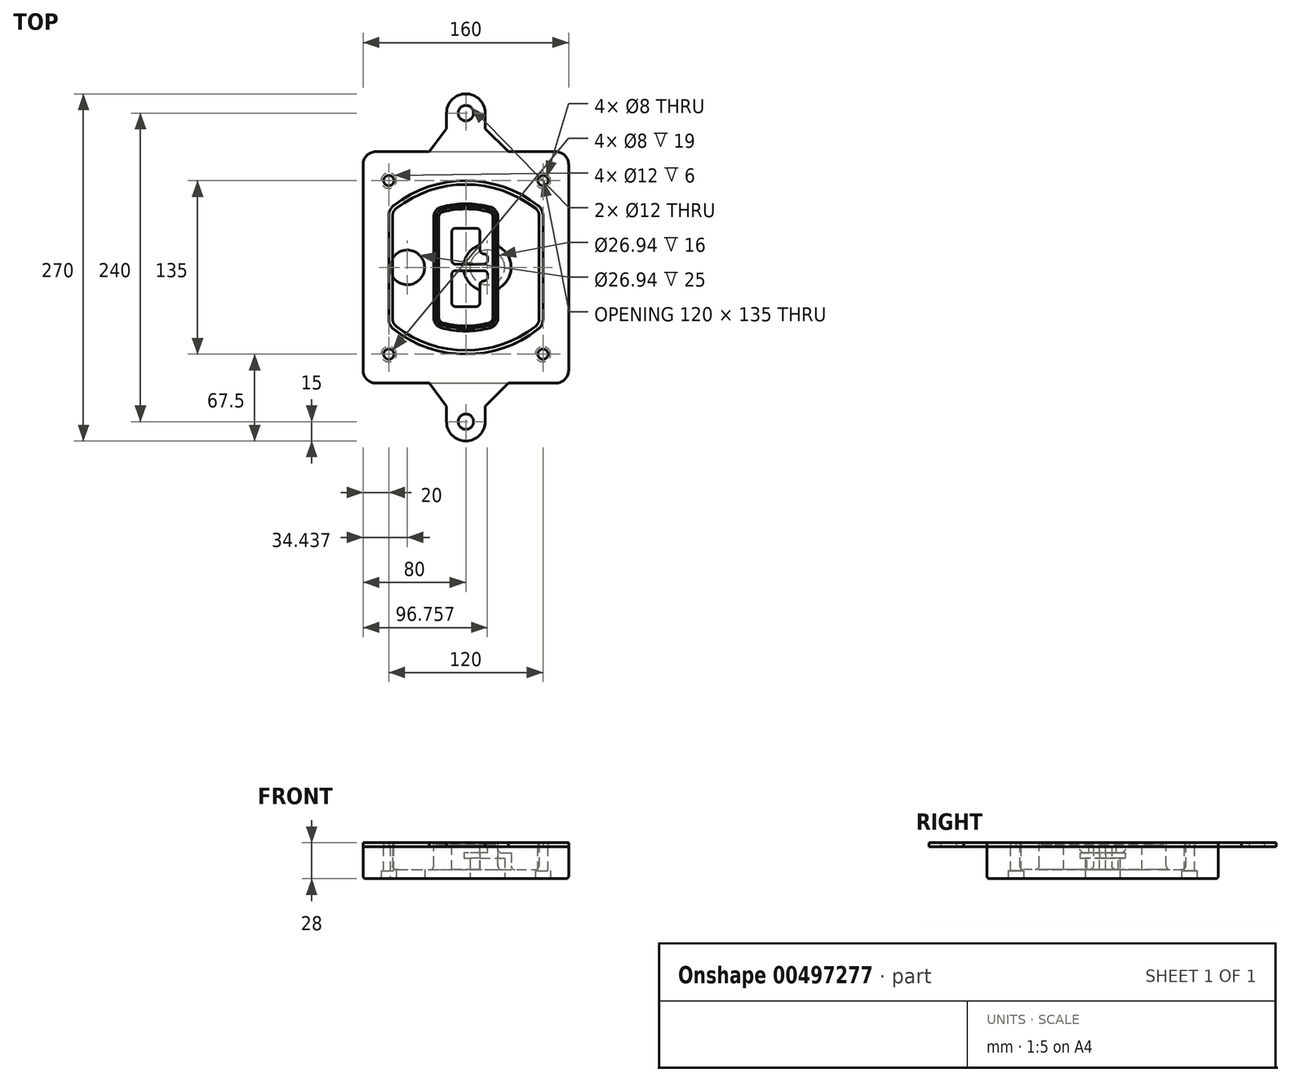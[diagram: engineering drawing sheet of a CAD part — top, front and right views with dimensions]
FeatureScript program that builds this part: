
annotation { "Feature Type Name" : "Feature", "Feature Type Description" : "" }
export const myFeature = defineFeature(function(context is Context, id is Id, definition is map)
    precondition{}
    {
        {
            var Q0;
            Q0=qCreatedBy(makeId("Top.planeOp"),FACE);
            var sketch = newSketch(context, id + "F0", { "sketchPlane" : qUnion([Q0])});
            skPoint(sketch, "E0.rect.middle", {"position": v(0, 0) * mm});
            skLineSegment(sketch, "E1.bottom", {"start": v(-70, -90) * mm, "end": v(70, -90) * mm});
            skLineSegment(sketch, "E1.top", {"start": v(-70, 90) * mm, "end": v(70, 90) * mm});
            skLineSegment(sketch, "E1.left", {"start": v(-80, -80) * mm, "end": v(-80, 80) * mm});
            skLineSegment(sketch, "E1.right", {"start": v(80, -80) * mm, "end": v(80, 80) * mm});
            skLineSegment(sketch, "E2", {"start": v(-80, 90) * mm, "end": v(80, -90) * mm, "construction": true});
            skLineSegment(sketch, "E3", {"start": v(80, 90) * mm, "end": v(-80, -90) * mm, "construction": true});
            skCircle(sketch, "E4", {"center": v(-60, 67.5) * mm, "radius": 4 * mm});
            skCircle(sketch, "E5", {"center": v(60, 67.5) * mm, "radius": 4 * mm});
            skCircle(sketch, "E6", {"center": v(60, -67.5) * mm, "radius": 4 * mm});
            skCircle(sketch, "E7", {"center": v(-60, -67.5) * mm, "radius": 4 * mm});
            skLineSegment(sketch, "E8", {"start": v(-60, 67.5) * mm, "end": v(60, 67.5) * mm, "construction": true});
            skLineSegment(sketch, "E9", {"start": v(60, 67.5) * mm, "end": v(60, -67.5) * mm, "construction": true});
            skLineSegment(sketch, "E10", {"start": v(60, -67.5) * mm, "end": v(-60, -67.5) * mm, "construction": true});
            skLineSegment(sketch, "E11", {"start": v(-60, -67.5) * mm, "end": v(-60, 67.5) * mm, "construction": true});
            skLineSegment(sketch, "E12", {"start": v(-60, 40.3) * mm, "end": v(-60, -40.3) * mm});
            skLineSegment(sketch, "E13", {"start": v(60, 40.3) * mm, "end": v(60, -40.3) * mm});
            skArc(sketch, "E14", {"start": v(56.15, 48.18) * mm, "mid": v(0, 67.5) * mm, "end": v(-56.15, 48.18) * mm});
            skArc(sketch, "E15", {"start": v(-56.15, -48.18) * mm, "mid": v(0, -67.5) * mm, "end": v(56.15, -48.18) * mm});
            skLineSegment(sketch, "E16", {"start": v(-60, 0) * mm, "end": v(60, 0) * mm, "construction": true});
            skPoint(sketch, "E17.visualSharp", {"position": v(-60, -45) * mm});
            skArc(sketch, "E17.filletArc", {"start": v(-60, -40.3) * mm, "mid": v(-58.99, -44.68) * mm, "end": v(-56.15, -48.18) * mm});
            skPoint(sketch, "E18.visualSharp", {"position": v(-60, 45) * mm});
            skArc(sketch, "E18.filletArc", {"start": v(-56.15, 48.18) * mm, "mid": v(-58.99, 44.68) * mm, "end": v(-60, 40.3) * mm});
            skPoint(sketch, "E19.visualSharp", {"position": v(60, 45) * mm});
            skArc(sketch, "E19.filletArc", {"start": v(60, 40.3) * mm, "mid": v(58.99, 44.68) * mm, "end": v(56.15, 48.18) * mm});
            skPoint(sketch, "E20.visualSharp", {"position": v(60, -45) * mm});
            skArc(sketch, "E20.filletArc", {"start": v(56.15, -48.18) * mm, "mid": v(58.99, -44.68) * mm, "end": v(60, -40.3) * mm});
            skPoint(sketch, "E21.visualSharp", {"position": v(-80, 90) * mm});
            skArc(sketch, "E21.filletArc", {"start": v(-70, 90) * mm, "mid": v(-77.07, 87.07) * mm, "end": v(-80, 80) * mm});
            skPoint(sketch, "E22.visualSharp", {"position": v(80, 90) * mm});
            skArc(sketch, "E22.filletArc", {"start": v(80, 80) * mm, "mid": v(77.07, 87.07) * mm, "end": v(70, 90) * mm});
            skPoint(sketch, "E23.visualSharp", {"position": v(80, -90) * mm});
            skArc(sketch, "E23.filletArc", {"start": v(70, -90) * mm, "mid": v(77.07, -87.07) * mm, "end": v(80, -80) * mm});
            skPoint(sketch, "E24.visualSharp", {"position": v(-80, -90) * mm});
            skArc(sketch, "E24.filletArc", {"start": v(-80, -80) * mm, "mid": v(-77.07, -87.07) * mm, "end": v(-70, -90) * mm});
            skArc(sketch, "E25.0", {"start": v(57, 40.3) * mm, "mid": v(56.3, 43.36) * mm, "end": v(54.3, 45.81) * mm});
            skLineSegment(sketch, "E25.1", {"start": v(57, 40.3) * mm, "end": v(57, -40.3) * mm});
            skArc(sketch, "E25.2", {"start": v(54.3, -45.81) * mm, "mid": v(56.3, -43.36) * mm, "end": v(57, -40.3) * mm});
            skArc(sketch, "E25.3", {"start": v(-54.3, -45.81) * mm, "mid": v(0, -64.5) * mm, "end": v(54.3, -45.81) * mm});
            skArc(sketch, "E25.4", {"start": v(-57, -40.3) * mm, "mid": v(-56.3, -43.36) * mm, "end": v(-54.3, -45.81) * mm});
            skArc(sketch, "E25.5", {"start": v(54.3, 45.81) * mm, "mid": v(0, 64.5) * mm, "end": v(-54.3, 45.81) * mm});
            skLineSegment(sketch, "E25.6", {"start": v(-57, 40.3) * mm, "end": v(-57, -40.3) * mm});
            skArc(sketch, "E25.7", {"start": v(-54.3, 45.81) * mm, "mid": v(-56.3, 43.36) * mm, "end": v(-57, 40.3) * mm});
            skArc(sketch, "E26.0", {"start": v(-58.62, 51.33) * mm, "mid": v(-62.58, 46.43) * mm, "end": v(-64, 40.3) * mm});
            skArc(sketch, "E26.1", {"start": v(58.62, 51.33) * mm, "mid": v(0, 71.5) * mm, "end": v(-58.62, 51.33) * mm});
            skArc(sketch, "E26.2", {"start": v(64, 40.3) * mm, "mid": v(62.58, 46.43) * mm, "end": v(58.62, 51.33) * mm});
            skLineSegment(sketch, "E26.3", {"start": v(64, 40.3) * mm, "end": v(64, -40.3) * mm});
            skArc(sketch, "E26.4", {"start": v(58.62, -51.33) * mm, "mid": v(62.58, -46.43) * mm, "end": v(64, -40.3) * mm});
            skLineSegment(sketch, "E26.5", {"start": v(-64, 40.3) * mm, "end": v(-64, -40.3) * mm});
            skArc(sketch, "E26.6", {"start": v(-58.62, -51.33) * mm, "mid": v(0, -71.5) * mm, "end": v(58.62, -51.33) * mm});
            skArc(sketch, "E26.7", {"start": v(-64, -40.3) * mm, "mid": v(-62.58, -46.43) * mm, "end": v(-58.62, -51.33) * mm});
            skSolve(sketch);
        }
        {
            var Q0;
            Q0=makeQuery(id+"F0.imprint","IMPRINT",FACE,{"disambiguationData":[TD([[makeQuery(id+"F0.imprint","IMPRINT",EDGE,{"derivedFrom":sQuery(id+"F0.wireOp",EDGE,"E1.bottom")}),1.0]])]});
            var Q1;
            Q1=makeQuery(id+"F0.imprint","IMPRINT",FACE,{"disambiguationData":[TD([[makeQuery(id+"F0.imprint","IMPRINT",EDGE,{"derivedFrom":sQuery(id+"F0.wireOp",EDGE,"E12")}),1.0]])]});
            var Q2;
            Q2=makeQuery(id+"F0.imprint","IMPRINT",FACE,{"disambiguationData":[TD([[makeQuery(id+"F0.imprint","IMPRINT",EDGE,{"derivedFrom":sQuery(id+"F0.wireOp",EDGE,"E25.0")}),1.0]])]});
            var Q3;
            Q3=makeQuery(id+"F0.imprint","IMPRINT",FACE,{"disambiguationData":[TD([[makeQuery(id+"F0.imprint","IMPRINT",EDGE,{"derivedFrom":sQuery(id+"F0.wireOp",EDGE,"E12")}),-1.0]])]});
            extrude(context, id + "F1", {"entities" : qUnion([Q0, Q1, Q2, Q3]), "oppositeDirection" : true, "depth" : 25 * mm});
        }
        {
            var Q0;
            Q0=makeQuery(id+"F0.imprint","IMPRINT",FACE,{"disambiguationData":[TD([[makeQuery(id+"F0.imprint","IMPRINT",EDGE,{"derivedFrom":sQuery(id+"F0.wireOp",EDGE,"E12")}),1.0]])]});
            extrude(context, id + "F2", {"entities" : qUnion([Q0]), "operationType" : NewBodyOperationType.ADD, "depth" : 3 * mm});
        }
        {
            var Q0;
            Q0=makeQuery(id+"F0.imprint","IMPRINT",FACE,{"disambiguationData":[TD([[makeQuery(id+"F0.imprint","IMPRINT",EDGE,{"derivedFrom":sQuery(id+"F0.wireOp",EDGE,"E25.0")}),1.0]])]});
            extrude(context, id + "F3", {"entities" : qUnion([Q0]), "operationType" : NewBodyOperationType.REMOVE, "oppositeDirection" : true, "depth" : 18 * mm});
        }
        {
            var Q0;
            Q0=makeQuery(id+"F2.opExtrude","CAP_FACE",FACE,{"disambiguationData":[OSD([sQuery(id+"F0.wireOp",EDGE,"E12"),sQuery(id+"F0.wireOp",EDGE,"E13"),sQuery(id+"F0.wireOp",EDGE,"E14"),sQuery(id+"F0.wireOp",EDGE,"E15"),sQuery(id+"F0.wireOp",EDGE,"E17.filletArc"),sQuery(id+"F0.wireOp",EDGE,"E18.filletArc"),sQuery(id+"F0.wireOp",EDGE,"E19.filletArc"),sQuery(id+"F0.wireOp",EDGE,"E20.filletArc"),sQuery(id+"F0.wireOp",EDGE,"E25.0"),sQuery(id+"F0.wireOp",EDGE,"E25.1"),sQuery(id+"F0.wireOp",EDGE,"E25.2"),sQuery(id+"F0.wireOp",EDGE,"E25.3"),sQuery(id+"F0.wireOp",EDGE,"E25.4"),sQuery(id+"F0.wireOp",EDGE,"E25.5"),sQuery(id+"F0.wireOp",EDGE,"E25.6"),sQuery(id+"F0.wireOp",EDGE,"E25.7")])],"isStart":false});
            var sketch = newSketch(context, id + "F4", { "sketchPlane" : qUnion([Q0])});
            skArc(sketch, "E27.0", {"start": v(-19.08, -46.97) * mm, "mid": v(0, -49.5) * mm, "end": v(19.08, -46.97) * mm});
            skArc(sketch, "E28.0", {"start": v(19.08, 46.97) * mm, "mid": v(0, 49.5) * mm, "end": v(-19.08, 46.97) * mm});
            skLineSegment(sketch, "E29", {"start": v(-25, 39.25) * mm, "end": v(-25, -39.25) * mm});
            skLineSegment(sketch, "E30", {"start": v(25, 39.25) * mm, "end": v(25, -39.25) * mm});
            skLineSegment(sketch, "E31", {"start": v(-25, 45.1) * mm, "end": v(25, 45.1) * mm, "construction": true});
            skLineSegment(sketch, "E32", {"start": v(-25, -45.1) * mm, "end": v(25, -45.1) * mm, "construction": true});
            skPoint(sketch, "E33.visualSharp", {"position": v(-25, 45.1) * mm});
            skArc(sketch, "E33.filletArc", {"start": v(-19.08, 46.97) * mm, "mid": v(-23.35, 44.11) * mm, "end": v(-25, 39.25) * mm});
            skPoint(sketch, "E34.visualSharp", {"position": v(25, 45.1) * mm});
            skArc(sketch, "E34.filletArc", {"start": v(25, 39.25) * mm, "mid": v(23.35, 44.11) * mm, "end": v(19.08, 46.97) * mm});
            skPoint(sketch, "E35.visualSharp", {"position": v(25, -45.1) * mm});
            skArc(sketch, "E35.filletArc", {"start": v(19.08, -46.97) * mm, "mid": v(23.35, -44.11) * mm, "end": v(25, -39.25) * mm});
            skPoint(sketch, "E36.visualSharp", {"position": v(-25, -45.1) * mm});
            skArc(sketch, "E36.filletArc", {"start": v(-25, -39.25) * mm, "mid": v(-23.35, -44.11) * mm, "end": v(-19.08, -46.97) * mm});
            skArc(sketch, "E37.0", {"start": v(54.3, 45.81) * mm, "mid": v(0, 64.5) * mm, "end": v(-54.3, 45.81) * mm});
            skArc(sketch, "E37.1", {"start": v(-54.3, 45.81) * mm, "mid": v(-56.3, 43.36) * mm, "end": v(-57, 40.3) * mm});
            skLineSegment(sketch, "E37.2", {"start": v(-57, 40.3) * mm, "end": v(-57, -40.3) * mm});
            skArc(sketch, "E37.3", {"start": v(-57, -40.3) * mm, "mid": v(-56.3, -43.36) * mm, "end": v(-54.3, -45.81) * mm});
            skArc(sketch, "E37.4", {"start": v(-54.3, -45.81) * mm, "mid": v(0, -64.5) * mm, "end": v(54.3, -45.81) * mm});
            skArc(sketch, "E37.5", {"start": v(54.3, -45.81) * mm, "mid": v(56.3, -43.36) * mm, "end": v(57, -40.3) * mm});
            skLineSegment(sketch, "E37.6", {"start": v(57, 40.3) * mm, "end": v(57, -40.3) * mm});
            skArc(sketch, "E37.7", {"start": v(57, 40.3) * mm, "mid": v(56.3, 43.36) * mm, "end": v(54.3, 45.81) * mm});
            skLineSegment(sketch, "E38.0", {"start": v(23, 39.25) * mm, "end": v(23, -39.25) * mm});
            skArc(sketch, "E38.1", {"start": v(18.56, -45.04) * mm, "mid": v(21.76, -42.9) * mm, "end": v(23, -39.25) * mm});
            skArc(sketch, "E38.2", {"start": v(-18.56, -45.04) * mm, "mid": v(0, -47.5) * mm, "end": v(18.56, -45.04) * mm});
            skArc(sketch, "E38.3", {"start": v(-23, -39.25) * mm, "mid": v(-21.76, -42.9) * mm, "end": v(-18.56, -45.04) * mm});
            skLineSegment(sketch, "E38.4", {"start": v(-23, 39.25) * mm, "end": v(-23, -39.25) * mm});
            skArc(sketch, "E38.5", {"start": v(23, 39.25) * mm, "mid": v(21.76, 42.9) * mm, "end": v(18.56, 45.04) * mm});
            skArc(sketch, "E38.6", {"start": v(-18.56, 45.04) * mm, "mid": v(-21.76, 42.9) * mm, "end": v(-23, 39.25) * mm});
            skArc(sketch, "E38.7", {"start": v(18.56, 45.04) * mm, "mid": v(0, 47.5) * mm, "end": v(-18.56, 45.04) * mm});
            skArc(sketch, "E39.0", {"start": v(21, 39.25) * mm, "mid": v(20.18, 41.68) * mm, "end": v(18.04, 43.1) * mm});
            skLineSegment(sketch, "E39.1", {"start": v(21, 39.25) * mm, "end": v(21, -39.25) * mm});
            skArc(sketch, "E39.2", {"start": v(18.04, -43.1) * mm, "mid": v(20.18, -41.68) * mm, "end": v(21, -39.25) * mm});
            skArc(sketch, "E39.3", {"start": v(-18.04, -43.1) * mm, "mid": v(0, -45.5) * mm, "end": v(18.04, -43.1) * mm});
            skArc(sketch, "E39.4", {"start": v(-21, -39.25) * mm, "mid": v(-20.18, -41.68) * mm, "end": v(-18.04, -43.1) * mm});
            skArc(sketch, "E39.5", {"start": v(18.04, 43.1) * mm, "mid": v(0, 45.5) * mm, "end": v(-18.04, 43.1) * mm});
            skLineSegment(sketch, "E39.6", {"start": v(-21, 39.25) * mm, "end": v(-21, -39.25) * mm});
            skArc(sketch, "E39.7", {"start": v(-18.04, 43.1) * mm, "mid": v(-20.18, 41.68) * mm, "end": v(-21, 39.25) * mm});
            skLineSegment(sketch, "E40", {"start": v(-25, 0) * mm, "end": v(25, 0) * mm, "construction": true});
            skLineSegment(sketch, "E41", {"start": v(-11, 5.5) * mm, "end": v(-11, 27.5) * mm});
            skLineSegment(sketch, "E42", {"start": v(-8, 30.5) * mm, "end": v(8, 30.5) * mm});
            skLineSegment(sketch, "E43", {"start": v(11, 27.5) * mm, "end": v(11, 13.5) * mm});
            skLineSegment(sketch, "E44", {"start": v(14, 10.5) * mm, "end": v(14, 10.5) * mm});
            skLineSegment(sketch, "E45", {"start": v(17, 7.5) * mm, "end": v(17, 5.5) * mm});
            skLineSegment(sketch, "E46", {"start": v(14, 2.5) * mm, "end": v(-8, 2.5) * mm});
            skPoint(sketch, "E47.visualSharp", {"position": v(-11, 30.5) * mm});
            skArc(sketch, "E47.filletArc", {"start": v(-8, 30.5) * mm, "mid": v(-10.12, 29.62) * mm, "end": v(-11, 27.5) * mm});
            skPoint(sketch, "E48.visualSharp", {"position": v(11, 30.5) * mm});
            skArc(sketch, "E48.filletArc", {"start": v(11, 27.5) * mm, "mid": v(10.12, 29.62) * mm, "end": v(8, 30.5) * mm});
            skPoint(sketch, "E49.visualSharp", {"position": v(11, 10.5) * mm});
            skArc(sketch, "E49.filletArc", {"start": v(11, 13.5) * mm, "mid": v(11.88, 11.38) * mm, "end": v(14, 10.5) * mm});
            skPoint(sketch, "E50.visualSharp", {"position": v(17, 10.5) * mm});
            skArc(sketch, "E50.filletArc", {"start": v(17, 7.5) * mm, "mid": v(16.12, 9.62) * mm, "end": v(14, 10.5) * mm});
            skPoint(sketch, "E51.visualSharp", {"position": v(17, 2.5) * mm});
            skArc(sketch, "E51.filletArc", {"start": v(14, 2.5) * mm, "mid": v(16.12, 3.38) * mm, "end": v(17, 5.5) * mm});
            skPoint(sketch, "E52.visualSharp", {"position": v(-11, 2.5) * mm});
            skArc(sketch, "E52.filletArc", {"start": v(-11, 5.5) * mm, "mid": v(-10.12, 3.38) * mm, "end": v(-8, 2.5) * mm});
            skLineSegment(sketch, "E53.0.MirrorCS", {"start": v(14, -2.5) * mm, "end": v(-8, -2.5) * mm});
            skArc(sketch, "E54.0.MirrorCS", {"start": v(-11, -5.5) * mm, "mid": v(-10.12, -3.38) * mm, "end": v(-8, -2.5) * mm});
            skLineSegment(sketch, "E55.0.MirrorCS", {"start": v(-11, -5.5) * mm, "end": v(-11, -27.5) * mm});
            skArc(sketch, "E56.0.MirrorCS", {"start": v(-8, -30.5) * mm, "mid": v(-10.12, -29.62) * mm, "end": v(-11, -27.5) * mm});
            skLineSegment(sketch, "E57.0.MirrorCS", {"start": v(-8, -30.5) * mm, "end": v(8, -30.5) * mm});
            skArc(sketch, "E58.0.MirrorCS", {"start": v(11, -27.5) * mm, "mid": v(10.12, -29.62) * mm, "end": v(8, -30.5) * mm});
            skLineSegment(sketch, "E59.0.MirrorCS", {"start": v(11, -27.5) * mm, "end": v(11, -13.5) * mm});
            skArc(sketch, "E60.0.MirrorCS", {"start": v(11, -13.5) * mm, "mid": v(11.88, -11.38) * mm, "end": v(14, -10.5) * mm});
            skArc(sketch, "E61.0.MirrorCS", {"start": v(17, -7.5) * mm, "mid": v(16.12, -9.62) * mm, "end": v(14, -10.5) * mm});
            skLineSegment(sketch, "E62.0.MirrorCS", {"start": v(17, -7.5) * mm, "end": v(17, -5.5) * mm});
            skArc(sketch, "E63.0.MirrorCS", {"start": v(14, -2.5) * mm, "mid": v(16.12, -3.38) * mm, "end": v(17, -5.5) * mm});
            skSolve(sketch);
        }
        {
            var Q0;
            Q0=makeQuery(id+"F4.imprint","IMPRINT",FACE,{"disambiguationData":[TD([[makeQuery(id+"F4.imprint","IMPRINT",EDGE,{"derivedFrom":sQuery(id+"F4.wireOp",EDGE,"E27.0")}),1.0]])]});
            var Q1;
            Q1=makeQuery(id+"F4.imprint","IMPRINT",FACE,{"disambiguationData":[TD([[makeQuery(id+"F4.imprint","IMPRINT",EDGE,{"derivedFrom":sQuery(id+"F4.wireOp",EDGE,"E38.0")}),-1.0]])]});
            var Q2;
            Q2=makeQuery(id+"F4.imprint","IMPRINT",FACE,{"disambiguationData":[TD([[makeQuery(id+"F4.imprint","IMPRINT",EDGE,{"derivedFrom":sQuery(id+"F4.wireOp",EDGE,"E39.0")}),1.0]])]});
            extrude(context, id + "F5", {"entities" : qUnion([Q0, Q1, Q2]), "operationType" : NewBodyOperationType.ADD, "endBound" : BoundingType.UP_TO_NEXT, "oppositeDirection" : true, "depth" : 25 * mm});
        }
        {
            var Q0;
            Q0=makeQuery(id+"F4.imprint","IMPRINT",FACE,{"disambiguationData":[TD([[makeQuery(id+"F4.imprint","IMPRINT",EDGE,{"derivedFrom":sQuery(id+"F4.wireOp",EDGE,"E38.0")}),-1.0]])]});
            extrude(context, id + "F6", {"entities" : qUnion([Q0]), "operationType" : NewBodyOperationType.REMOVE, "oppositeDirection" : true, "depth" : 2 * mm});
        }
        {
            var Q0;
            Q0=makeQuery(id+"F1.opExtrude","CAP_FACE",FACE,{"disambiguationData":[OSD([sQuery(id+"F0.wireOp",EDGE,"E1.bottom"),sQuery(id+"F0.wireOp",EDGE,"E1.top"),sQuery(id+"F0.wireOp",EDGE,"E1.left"),sQuery(id+"F0.wireOp",EDGE,"E1.right"),sQuery(id+"F0.wireOp",EDGE,"E4"),sQuery(id+"F0.wireOp",EDGE,"E5"),sQuery(id+"F0.wireOp",EDGE,"E6"),sQuery(id+"F0.wireOp",EDGE,"E7"),sQuery(id+"F0.wireOp",EDGE,"E21.filletArc"),sQuery(id+"F0.wireOp",EDGE,"E22.filletArc"),sQuery(id+"F0.wireOp",EDGE,"E23.filletArc"),sQuery(id+"F0.wireOp",EDGE,"E24.filletArc")])],"isStart":false});
            var sketch = newSketch(context, id + "F7", { "sketchPlane" : qUnion([Q0])});
            skCircle(sketch, "E64", {"center": v(16.76, 0) * mm, "radius": 13.47 * mm});
            skCircle(sketch, "E65", {"center": v(-45.56, 0) * mm, "radius": 13.47 * mm});
            skLineSegment(sketch, "E66", {"start": v(80, 0) * mm, "end": v(-80, 0) * mm});
            skCircle(sketch, "E67", {"center": v(16.76, 0) * mm, "radius": 18.47 * mm});
            skCircle(sketch, "E68", {"center": v(60, -67.5) * mm, "radius": 6 * mm});
            skCircle(sketch, "E69", {"center": v(-60, -67.5) * mm, "radius": 6 * mm});
            skCircle(sketch, "E70", {"center": v(-60, 67.5) * mm, "radius": 6 * mm});
            skCircle(sketch, "E71", {"center": v(60, 67.5) * mm, "radius": 6 * mm});
            skSolve(sketch);
        }
        {
            var Q0;
            {var subQ1=sQuery(id+"F7.wireOp",EDGE,"E66");var subQ4=sQuery(id+"F7.wireOp",EDGE,"E64");var subQ6=makeQuery(id+"F7.imprint","INTERSECT",VERTEX,{"disambiguationData":[OD(0.0)],"derivedFrom":[subQ4,subQ1]});Q0=makeQuery(id+"F7.imprint","IMPRINT",FACE,{"disambiguationData":[TD([[makeQuery(id+"F7.imprint","IMPRINT",EDGE,{"disambiguationData":[TD([[subQ6,-1.0]])],"derivedFrom":subQ4}),-1.0]])]});}
            var Q1;
            {var subQ0=sQuery(id+"F7.wireOp",EDGE,"E66");var subQ1=sQuery(id+"F7.wireOp",EDGE,"E64");var subQ3=makeQuery(id+"F7.imprint","INTERSECT",VERTEX,{"disambiguationData":[OD(0.0)],"derivedFrom":[subQ1,subQ0]});Q1=makeQuery(id+"F7.imprint","IMPRINT",FACE,{"disambiguationData":[TD([[makeQuery(id+"F7.imprint","IMPRINT",EDGE,{"disambiguationData":[TD([[subQ3,-1.0]])],"derivedFrom":subQ1}),1.0]])]});}
            var Q2;
            {var subQ0=sQuery(id+"F7.wireOp",EDGE,"E66");var subQ1=sQuery(id+"F7.wireOp",EDGE,"E64");var subQ3=makeQuery(id+"F7.imprint","INTERSECT",VERTEX,{"disambiguationData":[OD(0.0)],"derivedFrom":[subQ1,subQ0]});Q2=makeQuery(id+"F7.imprint","IMPRINT",FACE,{"disambiguationData":[TD([[makeQuery(id+"F7.imprint","IMPRINT",EDGE,{"disambiguationData":[TD([[subQ3,1.0]])],"derivedFrom":subQ1}),1.0]])]});}
            var Q3;
            {var subQ1=sQuery(id+"F7.wireOp",EDGE,"E66");var subQ4=sQuery(id+"F7.wireOp",EDGE,"E64");var subQ6=makeQuery(id+"F7.imprint","INTERSECT",VERTEX,{"disambiguationData":[OD(0.0)],"derivedFrom":[subQ4,subQ1]});Q3=makeQuery(id+"F7.imprint","IMPRINT",FACE,{"disambiguationData":[TD([[makeQuery(id+"F7.imprint","IMPRINT",EDGE,{"disambiguationData":[TD([[subQ6,1.0]])],"derivedFrom":subQ4}),-1.0]])]});}
            extrude(context, id + "F8", {"entities" : qUnion([Q0, Q1, Q2, Q3]), "operationType" : NewBodyOperationType.ADD, "oppositeDirection" : true, "depth" : 20 * mm});
        }
        {
            var Q0;
            {var subQ0=sQuery(id+"F7.wireOp",EDGE,"E66");var subQ1=sQuery(id+"F7.wireOp",EDGE,"E64");var subQ3=makeQuery(id+"F7.imprint","INTERSECT",VERTEX,{"disambiguationData":[OD(0.0)],"derivedFrom":[subQ1,subQ0]});Q0=makeQuery(id+"F7.imprint","IMPRINT",FACE,{"disambiguationData":[TD([[makeQuery(id+"F7.imprint","IMPRINT",EDGE,{"disambiguationData":[TD([[subQ3,-1.0]])],"derivedFrom":subQ1}),1.0]])]});}
            var Q1;
            {var subQ0=sQuery(id+"F7.wireOp",EDGE,"E66");var subQ1=sQuery(id+"F7.wireOp",EDGE,"E64");var subQ3=makeQuery(id+"F7.imprint","INTERSECT",VERTEX,{"disambiguationData":[OD(0.0)],"derivedFrom":[subQ1,subQ0]});Q1=makeQuery(id+"F7.imprint","IMPRINT",FACE,{"disambiguationData":[TD([[makeQuery(id+"F7.imprint","IMPRINT",EDGE,{"disambiguationData":[TD([[subQ3,1.0]])],"derivedFrom":subQ1}),1.0]])]});}
            extrude(context, id + "F9", {"entities" : qUnion([Q0, Q1]), "operationType" : NewBodyOperationType.REMOVE, "oppositeDirection" : true, "depth" : 16 * mm});
        }
        {
            var Q0;
            {var subQ0=sQuery(id+"F7.wireOp",EDGE,"E66");var subQ1=sQuery(id+"F7.wireOp",EDGE,"E65");var subQ3=makeQuery(id+"F7.imprint","INTERSECT",VERTEX,{"disambiguationData":[OD(0.0)],"derivedFrom":[subQ1,subQ0]});Q0=makeQuery(id+"F7.imprint","IMPRINT",FACE,{"disambiguationData":[TD([[makeQuery(id+"F7.imprint","IMPRINT",EDGE,{"disambiguationData":[TD([[subQ3,-1.0]])],"derivedFrom":subQ1}),1.0]])]});}
            var Q1;
            {var subQ0=sQuery(id+"F7.wireOp",EDGE,"E66");var subQ1=sQuery(id+"F7.wireOp",EDGE,"E65");var subQ3=makeQuery(id+"F7.imprint","INTERSECT",VERTEX,{"disambiguationData":[OD(0.0)],"derivedFrom":[subQ1,subQ0]});Q1=makeQuery(id+"F7.imprint","IMPRINT",FACE,{"disambiguationData":[TD([[makeQuery(id+"F7.imprint","IMPRINT",EDGE,{"disambiguationData":[TD([[subQ3,1.0]])],"derivedFrom":subQ1}),1.0]])]});}
            extrude(context, id + "F10", {"entities" : qUnion([Q0, Q1]), "operationType" : NewBodyOperationType.REMOVE, "oppositeDirection" : true, "depth" : 25 * mm});
        }
        {
            var Q0;
            Q0=makeQuery(id+"F7.imprint","IMPRINT",FACE,{"disambiguationData":[TD([[makeQuery(id+"F7.imprint","IMPRINT",EDGE,{"derivedFrom":sQuery(id+"F7.wireOp",EDGE,"E68")}),1.0]])]});
            var Q1;
            Q1=makeQuery(id+"F7.imprint","IMPRINT",FACE,{"disambiguationData":[TD([[makeQuery(id+"F7.imprint","IMPRINT",EDGE,{"derivedFrom":makeQuery(id+"F1.opExtrude","CAP_EDGE",EDGE,{"disambiguationData":[OSD([sQuery(id+"F0.wireOp",EDGE,"E5")])],"isStart":false})}),-1.0]])]});
            var Q2;
            Q2=makeQuery(id+"F7.imprint","IMPRINT",FACE,{"disambiguationData":[TD([[makeQuery(id+"F7.imprint","IMPRINT",EDGE,{"derivedFrom":sQuery(id+"F7.wireOp",EDGE,"E69")}),1.0]])]});
            var Q3;
            Q3=makeQuery(id+"F7.imprint","IMPRINT",FACE,{"disambiguationData":[TD([[makeQuery(id+"F7.imprint","IMPRINT",EDGE,{"derivedFrom":makeQuery(id+"F1.opExtrude","CAP_EDGE",EDGE,{"disambiguationData":[OSD([sQuery(id+"F0.wireOp",EDGE,"E4")])],"isStart":false})}),-1.0]])]});
            var Q4;
            Q4=makeQuery(id+"F7.imprint","IMPRINT",FACE,{"disambiguationData":[TD([[makeQuery(id+"F7.imprint","IMPRINT",EDGE,{"derivedFrom":sQuery(id+"F7.wireOp",EDGE,"E70")}),1.0]])]});
            var Q5;
            Q5=makeQuery(id+"F7.imprint","IMPRINT",FACE,{"disambiguationData":[TD([[makeQuery(id+"F7.imprint","IMPRINT",EDGE,{"derivedFrom":makeQuery(id+"F1.opExtrude","CAP_EDGE",EDGE,{"disambiguationData":[OSD([sQuery(id+"F0.wireOp",EDGE,"E7")])],"isStart":false})}),-1.0]])]});
            var Q6;
            Q6=makeQuery(id+"F7.imprint","IMPRINT",FACE,{"disambiguationData":[TD([[makeQuery(id+"F7.imprint","IMPRINT",EDGE,{"derivedFrom":sQuery(id+"F7.wireOp",EDGE,"E71")}),1.0]])]});
            var Q7;
            Q7=makeQuery(id+"F7.imprint","IMPRINT",FACE,{"disambiguationData":[TD([[makeQuery(id+"F7.imprint","IMPRINT",EDGE,{"derivedFrom":makeQuery(id+"F1.opExtrude","CAP_EDGE",EDGE,{"disambiguationData":[OSD([sQuery(id+"F0.wireOp",EDGE,"E6")])],"isStart":false})}),-1.0]])]});
            extrude(context, id + "F11", {"entities" : qUnion([Q0, Q1, Q2, Q3, Q4, Q5, Q6, Q7]), "operationType" : NewBodyOperationType.REMOVE, "oppositeDirection" : true, "depth" : 6 * mm});
        }
        {
            var Q0;
            Q0=makeQuery(id+"F9.boolean.opBoolean","COPY",FACE,{"derivedFrom":makeQuery(id+"F9.opExtrude","CAP_FACE",FACE,{"disambiguationData":[OSD([sQuery(id+"F7.wireOp",EDGE,"E64")])],"isStart":false})});
            var sketch = newSketch(context, id + "F12", { "sketchPlane" : qUnion([Q0])});
            skArc(sketch, "E72.0", {"start": v(11, 17.55) * mm, "mid": v(2.57, 11.82) * mm, "end": v(-1.54, 2.5) * mm});
            skArc(sketch, "E72.1", {"start": v(-1.54, -2.5) * mm, "mid": v(2.57, -11.82) * mm, "end": v(11, -17.55) * mm});
            skLineSegment(sketch, "E73", {"start": v(-1.54, -2.5) * mm, "end": v(14, -2.5) * mm});
            skLineSegment(sketch, "E74.0", {"start": v(14, 2.5) * mm, "end": v(-1.54, 2.5) * mm});
            skArc(sketch, "E74.1", {"start": v(14, 2.5) * mm, "mid": v(16.12, 3.38) * mm, "end": v(17, 5.5) * mm});
            skLineSegment(sketch, "E74.2", {"start": v(17, 7.5) * mm, "end": v(17, 5.5) * mm});
            skArc(sketch, "E74.3", {"start": v(17, 7.5) * mm, "mid": v(16.12, 9.62) * mm, "end": v(14, 10.5) * mm});
            skArc(sketch, "E74.4", {"start": v(11, 13.5) * mm, "mid": v(11.88, 11.38) * mm, "end": v(14, 10.5) * mm});
            skLineSegment(sketch, "E74.5", {"start": v(11, 17.55) * mm, "end": v(11, 13.5) * mm});
            skLineSegment(sketch, "E74.7", {"start": v(14, -2.5) * mm, "end": v(-1.54, -2.5) * mm});
            skArc(sketch, "E74.8", {"start": v(14, -2.5) * mm, "mid": v(16.12, -3.38) * mm, "end": v(17, -5.5) * mm});
            skLineSegment(sketch, "E74.9", {"start": v(17, -7.5) * mm, "end": v(17, -5.5) * mm});
            skArc(sketch, "E74.10", {"start": v(17, -7.5) * mm, "mid": v(16.12, -9.62) * mm, "end": v(14, -10.5) * mm});
            skArc(sketch, "E74.11", {"start": v(11, -13.5) * mm, "mid": v(11.88, -11.38) * mm, "end": v(14, -10.5) * mm});
            skLineSegment(sketch, "E74.12", {"start": v(11, -17.55) * mm, "end": v(11, -13.5) * mm});
            skPoint(sketch, "E75.orphan", {"position": v(11, -27.5) * mm});
            skPoint(sketch, "E76.orphan", {"position": v(-8, -2.5) * mm});
            skPoint(sketch, "E77.orphan", {"position": v(-8, 2.5) * mm});
            skPoint(sketch, "E78.orphan", {"position": v(11, 27.5) * mm});
            skSolve(sketch);
        }
        {
            var Q0;
            {var subQ7=sQuery(id+"F12.wireOp",EDGE,"E72.0");var subQ14=sQuery(id+"F12.wireOp",EDGE,"E72.1");var subQ16=sQuery(id+"F12.wireOp",EDGE,"E74.1");var subQ18=sQuery(id+"F12.wireOp",EDGE,"E74.8");Q0=qUnion([makeQuery(id+"F12.imprint","IMPRINT",FACE,{"disambiguationData":[TD([[makeQuery(id+"F12.imprint","IMPRINT",EDGE,{"derivedFrom":subQ7}),1.0]])]}),makeQuery(id+"F12.imprint","IMPRINT",FACE,{"disambiguationData":[TD([[makeQuery(id+"F12.imprint","IMPRINT",EDGE,{"derivedFrom":subQ14}),1.0]])]}),makeQuery(id+"F12.imprint","IMPRINT",FACE,{"disambiguationData":[TD([[makeQuery(id+"F12.imprint","IMPRINT",EDGE,{"derivedFrom":subQ16}),1.0]])]}),makeQuery(id+"F12.imprint","IMPRINT",FACE,{"disambiguationData":[TD([[makeQuery(id+"F12.imprint","IMPRINT",EDGE,{"derivedFrom":subQ18}),-1.0]])]})]);}
            var Q1;
            Q1=makeQuery(id+"F5.boolean.opBoolean","SPLIT",FACE,{"disambiguationData":[TD([makeQuery(id+"F5.opExtrude","SWEPT_FACE",FACE,{"disambiguationData":[OSD([sQuery(id+"F4.wireOp",EDGE,"E41")])]})])],"derivedFrom":makeQuery(id+"F3.boolean.opBoolean","COPY",FACE,{"derivedFrom":makeQuery(id+"F3.opExtrude","CAP_FACE",FACE,{"disambiguationData":[OSD([sQuery(id+"F0.wireOp",EDGE,"E25.0"),sQuery(id+"F0.wireOp",EDGE,"E25.1"),sQuery(id+"F0.wireOp",EDGE,"E25.2"),sQuery(id+"F0.wireOp",EDGE,"E25.3"),sQuery(id+"F0.wireOp",EDGE,"E25.4"),sQuery(id+"F0.wireOp",EDGE,"E25.5"),sQuery(id+"F0.wireOp",EDGE,"E25.6"),sQuery(id+"F0.wireOp",EDGE,"E25.7")])],"isStart":false})})});
            extrude(context, id + "F13", {"entities" : qUnion([Q0]), "operationType" : NewBodyOperationType.REMOVE, "endBound" : BoundingType.UP_TO_SURFACE, "endBoundEntityFace" : qUnion([Q1]), "depth" : 25 * mm});
        }
        {
            var Q0;
            Q0=makeQuery(id+"F3.boolean.opBoolean","COPY",EDGE,{"derivedFrom":makeQuery(id+"F3.opExtrude","CAP_EDGE",EDGE,{"disambiguationData":[OSD([sQuery(id+"F0.wireOp",EDGE,"E25.6")])],"isStart":false})});
            var Q1;
            Q1=makeQuery(id+"F8.boolean.opBoolean","INTERSECT",EDGE,{"derivedFrom":[makeQuery(id+"F5.opExtrude","SWEPT_FACE",FACE,{"disambiguationData":[OSD([sQuery(id+"F4.wireOp",EDGE,"E30")])]}),makeQuery(id+"F8.opExtrude","CAP_FACE",FACE,{"disambiguationData":[OSD([sQuery(id+"F7.wireOp",EDGE,"E67")])],"isStart":false})]});
            var Q2;
            Q2=makeQuery(id+"F8.boolean.opBoolean","INTERSECT",EDGE,{"disambiguationData":[OD(1.0)],"derivedFrom":[makeQuery(id+"F5.opExtrude","SWEPT_FACE",FACE,{"disambiguationData":[OSD([sQuery(id+"F4.wireOp",EDGE,"E30")])]}),makeQuery(id+"F8.opExtrude","SWEPT_FACE",FACE,{"disambiguationData":[OSD([sQuery(id+"F7.wireOp",EDGE,"E67")])]})]});
            var Q3;
            {var subQ0=sQuery(id+"F4.wireOp",EDGE,"E30");Q3=makeQuery(id+"F8.boolean.opBoolean","SPLIT",EDGE,{"disambiguationData":[TD([makeQuery(id+"F5.opExtrude","SWEPT_FACE",FACE,{"disambiguationData":[OSD([sQuery(id+"F4.wireOp",EDGE,"E35.filletArc")])]})])],"derivedFrom":makeQuery(id+"F5.opExtrude","CAP_EDGE",EDGE,{"disambiguationData":[OSD([subQ0])],"isStart":false})});}
            var Q4;
            {var subQ0=sQuery(id+"F0.wireOp",EDGE,"E25.7");var subQ1=sQuery(id+"F0.wireOp",EDGE,"E25.1");var subQ2=sQuery(id+"F0.wireOp",EDGE,"E25.6");var subQ3=sQuery(id+"F0.wireOp",EDGE,"E25.5");var subQ4=sQuery(id+"F0.wireOp",EDGE,"E25.4");var subQ5=sQuery(id+"F0.wireOp",EDGE,"E25.0");var subQ6=sQuery(id+"F0.wireOp",EDGE,"E25.2");var subQ7=sQuery(id+"F0.wireOp",EDGE,"E25.3");Q4=makeQuery(id+"F8.boolean.opBoolean","INTERSECT",EDGE,{"derivedFrom":[makeQuery(id+"F5.boolean.opBoolean","SPLIT",FACE,{"disambiguationData":[TD([makeQuery(id+"F2.opExtrude","SWEPT_FACE",FACE,{"disambiguationData":[OSD([subQ5])]})])],"derivedFrom":makeQuery(id+"F3.boolean.opBoolean","COPY",FACE,{"derivedFrom":makeQuery(id+"F3.opExtrude","CAP_FACE",FACE,{"disambiguationData":[OSD([subQ5,subQ1,subQ6,subQ7,subQ4,subQ3,subQ2,subQ0])],"isStart":false})})}),makeQuery(id+"F8.opExtrude","SWEPT_FACE",FACE,{"disambiguationData":[OSD([sQuery(id+"F7.wireOp",EDGE,"E67")])]})]});}
            var Q5;
            Q5=makeQuery(id+"F8.boolean.opBoolean","INTERSECT",EDGE,{"disambiguationData":[OD(0.0)],"derivedFrom":[makeQuery(id+"F5.opExtrude","SWEPT_FACE",FACE,{"disambiguationData":[OSD([sQuery(id+"F4.wireOp",EDGE,"E30")])]}),makeQuery(id+"F8.opExtrude","SWEPT_FACE",FACE,{"disambiguationData":[OSD([sQuery(id+"F7.wireOp",EDGE,"E67")])]})]});
            fillet(context, id + "F14", {"entities" : qUnion([Q0, Q1, Q2, Q3, Q4, Q5]), "radius" : 3 * mm, "tangentPropagation" : true, "allowEdgeOverflow" : false});
        }
        {
            var Q0;
            Q0=makeQuery(id+"F1.opExtrude","CAP_EDGE",EDGE,{"disambiguationData":[OSD([sQuery(id+"F0.wireOp",EDGE,"E1.bottom")])],"isStart":false});
            fillet(context, id + "F15", {"entities" : qUnion([Q0]), "radius" : 2 * mm, "tangentPropagation" : true, "allowEdgeOverflow" : false});
        }
        {
            var Q0;
            {var subQ0=sQuery(id+"F0.wireOp",EDGE,"E21.filletArc");var subQ1=sQuery(id+"F0.wireOp",EDGE,"E7");var subQ2=sQuery(id+"F0.wireOp",EDGE,"E6");var subQ3=sQuery(id+"F0.wireOp",EDGE,"E5");var subQ4=sQuery(id+"F0.wireOp",EDGE,"E4");var subQ5=sQuery(id+"F0.wireOp",EDGE,"E22.filletArc");var subQ6=sQuery(id+"F0.wireOp",EDGE,"E1.bottom");var subQ7=sQuery(id+"F0.wireOp",EDGE,"E1.right");var subQ8=sQuery(id+"F0.wireOp",EDGE,"E1.top");var subQ9=sQuery(id+"F0.wireOp",EDGE,"E1.left");var subQ10=sQuery(id+"F0.wireOp",EDGE,"E23.filletArc");var subQ11=sQuery(id+"F0.wireOp",EDGE,"E24.filletArc");Q0=makeQuery(id+"F2.boolean.opBoolean","SPLIT",FACE,{"disambiguationData":[TD([makeQuery(id+"F1.opExtrude","SWEPT_FACE",FACE,{"disambiguationData":[OSD([subQ6])]})])],"derivedFrom":makeQuery(id+"F1.opExtrude","CAP_FACE",FACE,{"disambiguationData":[OSD([subQ6,subQ8,subQ9,subQ7,subQ4,subQ3,subQ2,subQ1,subQ0,subQ5,subQ10,subQ11])],"isStart":true})});}
            var sketch = newSketch(context, id + "F16", { "sketchPlane" : qUnion([Q0])});
            skLineSegment(sketch, "E79.0", {"start": v(-70, 90) * mm, "end": v(70, 90) * mm});
            skArc(sketch, "E79.1", {"start": v(80, 80) * mm, "mid": v(77.07, 87.07) * mm, "end": v(70, 90) * mm});
            skCircle(sketch, "E79.2", {"center": v(60, 67.5) * mm, "radius": 4 * mm});
            skLineSegment(sketch, "E79.3", {"start": v(80, -80) * mm, "end": v(80, 80) * mm});
            skArc(sketch, "E79.4", {"start": v(60, 40.3) * mm, "mid": v(58.99, 44.68) * mm, "end": v(56.15, 48.18) * mm});
            skArc(sketch, "E79.5", {"start": v(56.15, 48.18) * mm, "mid": v(0, 67.5) * mm, "end": v(-56.15, 48.18) * mm});
            skLineSegment(sketch, "E79.6", {"start": v(60, 40.3) * mm, "end": v(60, -40.3) * mm});
            skCircle(sketch, "E79.7", {"center": v(-60, 67.5) * mm, "radius": 4 * mm});
            skArc(sketch, "E79.8", {"start": v(-70, 90) * mm, "mid": v(-77.07, 87.07) * mm, "end": v(-80, 80) * mm});
            skLineSegment(sketch, "E79.9", {"start": v(-80, -80) * mm, "end": v(-80, 80) * mm});
            skLineSegment(sketch, "E79.10", {"start": v(-60, 40.3) * mm, "end": v(-60, -40.3) * mm});
            skArc(sketch, "E79.11", {"start": v(-56.15, 48.18) * mm, "mid": v(-58.99, 44.68) * mm, "end": v(-60, 40.3) * mm});
            skCircle(sketch, "E79.12", {"center": v(-60, -67.5) * mm, "radius": 4 * mm});
            skArc(sketch, "E79.13", {"start": v(-60, -40.3) * mm, "mid": v(-58.99, -44.68) * mm, "end": v(-56.15, -48.18) * mm});
            skArc(sketch, "E79.14", {"start": v(-56.15, -48.18) * mm, "mid": v(0, -67.5) * mm, "end": v(56.15, -48.18) * mm});
            skLineSegment(sketch, "E79.15", {"start": v(-70, -90) * mm, "end": v(70, -90) * mm});
            skArc(sketch, "E79.16", {"start": v(-80, -80) * mm, "mid": v(-77.07, -87.07) * mm, "end": v(-70, -90) * mm});
            skCircle(sketch, "E79.17", {"center": v(60, -67.5) * mm, "radius": 4 * mm});
            skArc(sketch, "E79.18", {"start": v(70, -90) * mm, "mid": v(77.07, -87.07) * mm, "end": v(80, -80) * mm});
            skArc(sketch, "E79.19", {"start": v(56.15, -48.18) * mm, "mid": v(58.99, -44.68) * mm, "end": v(60, -40.3) * mm});
            skLineSegment(sketch, "E80", {"start": v(-28.56, 90) * mm, "end": v(-15, 108) * mm});
            skLineSegment(sketch, "E81", {"start": v(-15, 108) * mm, "end": v(-15, 120) * mm});
            skLineSegment(sketch, "E82", {"start": v(33, 90) * mm, "end": v(15, 108) * mm});
            skLineSegment(sketch, "E83", {"start": v(15, 108) * mm, "end": v(15, 120) * mm});
            skArc(sketch, "E84", {"start": v(15, 120) * mm, "mid": v(0, 135) * mm, "end": v(-15, 120) * mm});
            skCircle(sketch, "E85", {"center": v(0, 120) * mm, "radius": 6 * mm});
            skLineSegment(sketch, "E86", {"start": v(0, 120) * mm, "end": v(0, 90) * mm, "construction": true});
            skLineSegment(sketch, "E87", {"start": v(-80, 0) * mm, "end": v(80, 0) * mm, "construction": true});
            skLineSegment(sketch, "E88.MirrorCS", {"start": v(15, -108) * mm, "end": v(15, -120) * mm});
            skLineSegment(sketch, "E89.MirrorCS", {"start": v(-15, -108) * mm, "end": v(-15, -120) * mm});
            skLineSegment(sketch, "E90.MirrorCS", {"start": v(33, -90) * mm, "end": v(15, -108) * mm});
            skArc(sketch, "E91.MirrorCS", {"start": v(15, -120) * mm, "mid": v(0, -135) * mm, "end": v(-15, -120) * mm});
            skCircle(sketch, "E92.MirrorC", {"center": v(0, -120) * mm, "radius": 6 * mm});
            skLineSegment(sketch, "E93.MirrorCS", {"start": v(-28.56, -90) * mm, "end": v(-15, -108) * mm});
            skLineSegment(sketch, "E94.MirrorCS", {"start": v(0, -120) * mm, "end": v(0, -90) * mm, "construction": true});
            skSolve(sketch);
        }
        {
            var Q0;
            Q0 = qSketchRegion(id + "F16", true);
            var Q1;
            Q1=makeQuery(id+"F2.opExtrude","CAP_FACE",FACE,{"disambiguationData":[OSD([sQuery(id+"F0.wireOp",EDGE,"E12"),sQuery(id+"F0.wireOp",EDGE,"E13"),sQuery(id+"F0.wireOp",EDGE,"E14"),sQuery(id+"F0.wireOp",EDGE,"E15"),sQuery(id+"F0.wireOp",EDGE,"E17.filletArc"),sQuery(id+"F0.wireOp",EDGE,"E18.filletArc"),sQuery(id+"F0.wireOp",EDGE,"E19.filletArc"),sQuery(id+"F0.wireOp",EDGE,"E20.filletArc"),sQuery(id+"F0.wireOp",EDGE,"E25.0"),sQuery(id+"F0.wireOp",EDGE,"E25.1"),sQuery(id+"F0.wireOp",EDGE,"E25.2"),sQuery(id+"F0.wireOp",EDGE,"E25.3"),sQuery(id+"F0.wireOp",EDGE,"E25.4"),sQuery(id+"F0.wireOp",EDGE,"E25.5"),sQuery(id+"F0.wireOp",EDGE,"E25.6"),sQuery(id+"F0.wireOp",EDGE,"E25.7")])],"isStart":false});
            extrude(context, id + "F17", {"entities" : qUnion([Q0]), "endBound" : BoundingType.UP_TO_SURFACE, "endBoundEntityFace" : qUnion([Q1]), "depth" : 25 * mm});
        }
    });
